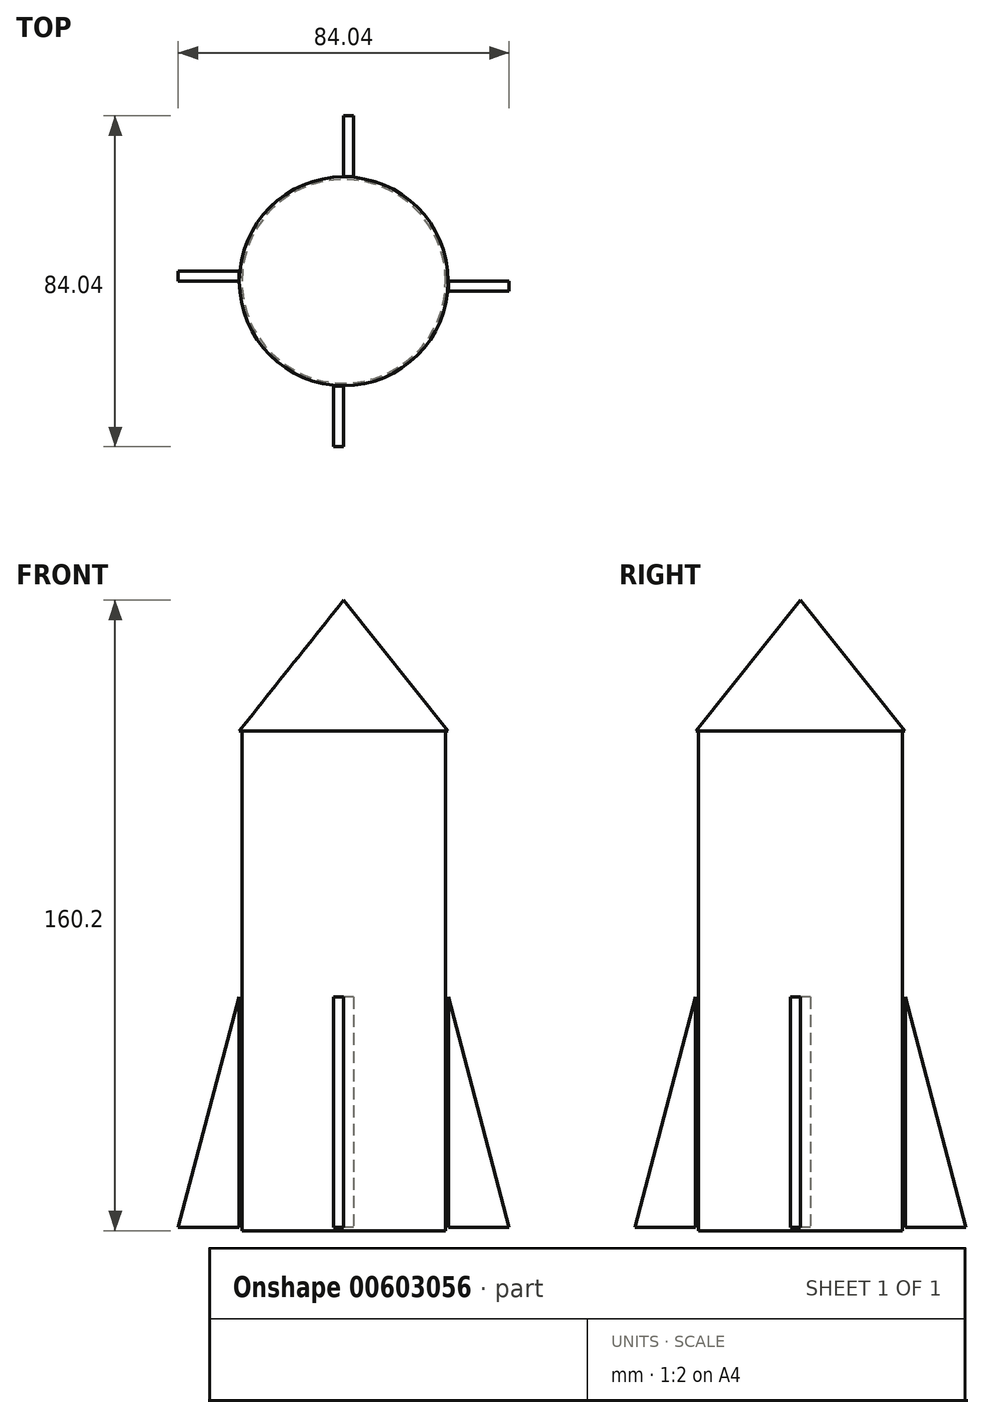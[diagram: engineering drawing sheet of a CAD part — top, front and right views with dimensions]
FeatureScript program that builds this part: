
annotation { "Feature Type Name" : "Feature", "Feature Type Description" : "" }
export const myFeature = defineFeature(function(context is Context, id is Id, definition is map)
    precondition{}
    {
        {
            var Q0;
            Q0=qCreatedBy(makeId("Top.planeOp"),FACE);
            var sketch = newSketch(context, id + "F0", { "sketchPlane" : qUnion([Q0])});
            skCircle(sketch, "E0", {"center": v(0, 0) * mm, "radius": 25.86 * mm});
            skSolve(sketch);
        }
        {
            var Q0;
            Q0=makeQuery(id+"F0.imprint","IMPRINT",FACE,{"disambiguationData":[TD([[makeQuery(id+"F0.imprint","IMPRINT",EDGE,{"derivedFrom":sQuery(id+"F0.wireOp",EDGE,"E0")}),1.0]])]});
            extrude(context, id + "F1", {"entities" : qUnion([Q0]), "oppositeDirection" : true, "depth" : 127 * mm, "offsetDistance" : 25.4 * mm});
        }
        {
            var Q0;
            Q0=qCreatedBy(makeId("Front.planeOp"),FACE);
            var sketch = newSketch(context, id + "F2", { "sketchPlane" : qUnion([Q0])});
            skLineSegment(sketch, "E1", {"start": v(0, 33.2) * mm, "end": v(0, -126.97) * mm});
            skLineSegment(sketch, "E2", {"start": v(0, 33.2) * mm, "end": v(26.54, 0) * mm});
            skLineSegment(sketch, "E3", {"start": v(0, 0) * mm, "end": v(26.54, 0) * mm});
            skSolve(sketch);
        }
        {
            var Q0;
            Q0 = qSketchRegion(id + "F2", true);
            var Q1;
            Q1=sQuery(id+"F2.wireOp",EDGE,"E1");
            revolve(context, id + "F3", {"operationType" : NewBodyOperationType.ADD, "entities" : qUnion([Q0]), "axis" : qUnion([Q1]), "revolveType" : RevolveType.FULL});
        }
        {
            var Q0;
            Q0=qCreatedBy(makeId("Front.planeOp"),FACE);
            var sketch = newSketch(context, id + "F4", { "sketchPlane" : qUnion([Q0])});
            skLineSegment(sketch, "E4", {"start": v(0, 33.6) * mm, "end": v(0, -126.13) * mm});
            skLineSegment(sketch, "E5", {"start": v(0, -126.13) * mm, "end": v(42.02, -126.13) * mm});
            skLineSegment(sketch, "E6", {"start": v(42.02, -126.13) * mm, "end": v(0, 33.6) * mm});
            skLineSegment(sketch, "E7", {"start": v(26.63, -67.61) * mm, "end": v(26.63, -126.13) * mm});
            skSolve(sketch);
        }
        {
            var Q0;
            {var subQ3=sQuery(id+"F4.wireOp",EDGE,"E7");Q0=makeQuery(id+"F4.imprint","IMPRINT",FACE,{"disambiguationData":[TD([[makeQuery(id+"F4.imprint","IMPRINT",EDGE,{"derivedFrom":subQ3}),1.0]])]});}
            extrude(context, id + "F5", {"entities" : qUnion([Q0]), "operationType" : NewBodyOperationType.ADD, "depth" : 2.54 * mm, "offsetDistance" : 25.4 * mm});
        }
        {
            var Q0;
            Q0=makeQuery(id+"F5.opExtrude","SWEPT_BODY",BODY,{"disambiguationData":[OSD([sQuery(id+"F4.wireOp",EDGE,"E5"),sQuery(id+"F4.wireOp",EDGE,"E6"),sQuery(id+"F4.wireOp",EDGE,"E7")])]});
            var Q1;
            Q1=makeQuery(id+"F1.opExtrude","SWEPT_FACE",FACE,{"disambiguationData":[OSD([sQuery(id+"F0.wireOp",EDGE,"E0")])]});
            circularPattern(context, id + "F6", {"entities" : qUnion([Q0]), "axis" : qUnion([Q1]), "angle" : 360 * degree, "instanceCount" : 4, "equalSpace" : true});
        }
    });
